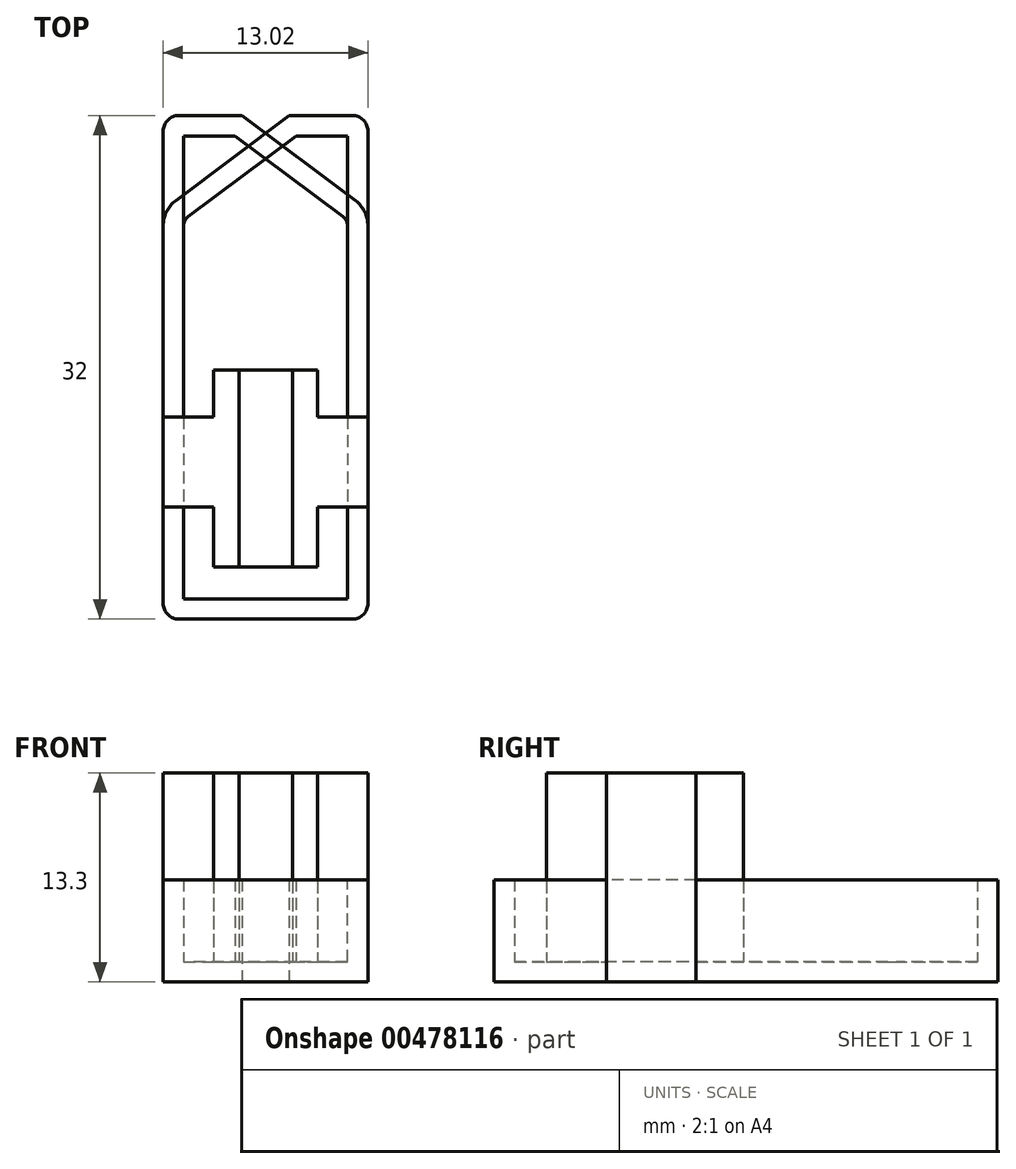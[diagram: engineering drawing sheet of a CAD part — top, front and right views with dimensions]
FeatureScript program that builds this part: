
annotation { "Feature Type Name" : "Feature", "Feature Type Description" : "" }
export const myFeature = defineFeature(function(context is Context, id is Id, definition is map)
    precondition{}
    {
        {
            var Q0;
            Q0=qCreatedBy(makeId("Top.planeOp"),FACE);
            var sketch = newSketch(context, id + "F0", { "sketchPlane" : qUnion([Q0])});
            skLineSegment(sketch, "E0.top", {"start": v(5.5, -13) * mm, "end": v(-5.5, -13) * mm});
            skLineSegment(sketch, "E0.left", {"start": v(6.5, 12) * mm, "end": v(6.5, -12) * mm});
            skLineSegment(sketch, "E0.right", {"start": v(-6.5, 13) * mm, "end": v(-6.5, -12) * mm});
            skPoint(sketch, "E0.middle", {"position": v(0, 0) * mm});
            skLineSegment(sketch, "E1", {"start": v(-6.5, 13) * mm, "end": v(-6.5, 18) * mm});
            skLineSegment(sketch, "E2", {"start": v(-5.5, 19) * mm, "end": v(-1.5, 19) * mm});
            skLineSegment(sketch, "E3", {"start": v(-1.5, 19) * mm, "end": v(5.7, 13.6) * mm});
            skPoint(sketch, "E4.visualSharp", {"position": v(6.5, 13) * mm});
            skArc(sketch, "E4.filletArc", {"start": v(6.5, 12) * mm, "mid": v(6.29, 12.9) * mm, "end": v(5.7, 13.6) * mm});
            skPoint(sketch, "E5.visualSharp", {"position": v(6.5, -13) * mm});
            skArc(sketch, "E5.filletArc", {"start": v(5.5, -13) * mm, "mid": v(6.2, -12.7) * mm, "end": v(6.5, -12) * mm});
            skPoint(sketch, "E6.visualSharp", {"position": v(-6.5, -13) * mm});
            skArc(sketch, "E6.filletArc", {"start": v(-6.5, -12) * mm, "mid": v(-6.2, -12.7) * mm, "end": v(-5.5, -13) * mm});
            skPoint(sketch, "E7.visualSharp", {"position": v(-6.5, 19) * mm});
            skArc(sketch, "E7.filletArc", {"start": v(-5.5, 19) * mm, "mid": v(-6.2, 18.7) * mm, "end": v(-6.5, 18) * mm});
            skSolve(sketch);
        }
        {
            var Q0;
            Q0 = qSketchRegion(id + "F0", true);
            extrude(context, id + "F1", {"entities" : qUnion([Q0]), "depth" : 6.5 * mm});
        }
        {
            var Q0;
            Q0=makeQuery(id+"F1.opExtrude","CAP_FACE",FACE,{"disambiguationData":[OSD([sQuery(id+"F0.wireOp",EDGE,"E0.top"),sQuery(id+"F0.wireOp",EDGE,"E0.left"),sQuery(id+"F0.wireOp",EDGE,"E0.right"),sQuery(id+"F0.wireOp",EDGE,"E1"),sQuery(id+"F0.wireOp",EDGE,"E2"),sQuery(id+"F0.wireOp",EDGE,"E3"),sQuery(id+"F0.wireOp",EDGE,"E4.filletArc"),sQuery(id+"F0.wireOp",EDGE,"E5.filletArc"),sQuery(id+"F0.wireOp",EDGE,"E6.filletArc"),sQuery(id+"F0.wireOp",EDGE,"E7.filletArc")])],"isStart":false});
            shell(context, id + "F2", {"entities" : qUnion([Q0]), "thickness" : 1.3 * mm});
        }
        {
            var Q0;
            Q0=qCreatedBy(makeId("Top.planeOp"),FACE);
            var sketch = newSketch(context, id + "F3", { "sketchPlane" : qUnion([Q0])});
            skLineSegment(sketch, "E8", {"start": v(1.7, -9.67) * mm, "end": v(1.7, 2.83) * mm});
            skLineSegment(sketch, "E9", {"start": v(1.7, 2.83) * mm, "end": v(-3.3, 2.83) * mm});
            skLineSegment(sketch, "E10", {"start": v(-3.3, 2.83) * mm, "end": v(-3.3, -0.17) * mm});
            skLineSegment(sketch, "E11", {"start": v(-3.3, -0.17) * mm, "end": v(-6.51, -0.17) * mm});
            skLineSegment(sketch, "E12", {"start": v(-6.51, -0.17) * mm, "end": v(-6.51, -5.87) * mm});
            skLineSegment(sketch, "E13", {"start": v(-6.51, -5.87) * mm, "end": v(-3.3, -5.87) * mm});
            skLineSegment(sketch, "E14", {"start": v(-3.3, -5.87) * mm, "end": v(-3.3, -9.67) * mm});
            skLineSegment(sketch, "E15", {"start": v(-3.3, -9.67) * mm, "end": v(1.7, -9.67) * mm});
            skSolve(sketch);
        }
        {
            var Q0;
            Q0 = qSketchRegion(id + "F3", true);
            var Q1;
            Q1 = qSketchRegion(id + "F5", true);
            extrude(context, id + "F4", {"entities" : qUnion([Q0, Q1]), "operationType" : NewBodyOperationType.ADD, "depth" : 13.3 * mm});
        }
        {
            var Q0;
            Q0=qCreatedBy(makeId("Top.planeOp"),FACE);
            var sketch = newSketch(context, id + "F5", { "sketchPlane" : qUnion([Q0])});
            skSolve(sketch);
        }
        {
            var Q0;
            Q0=makeQuery(id+"F1.opExtrude","SWEPT_BODY",BODY,{"disambiguationData":[OSD([sQuery(id+"F0.wireOp",EDGE,"E0.top"),sQuery(id+"F0.wireOp",EDGE,"E0.left"),sQuery(id+"F0.wireOp",EDGE,"E0.right"),sQuery(id+"F0.wireOp",EDGE,"E1"),sQuery(id+"F0.wireOp",EDGE,"E2"),sQuery(id+"F0.wireOp",EDGE,"E3"),sQuery(id+"F0.wireOp",EDGE,"E4.filletArc"),sQuery(id+"F0.wireOp",EDGE,"E5.filletArc"),sQuery(id+"F0.wireOp",EDGE,"E6.filletArc"),sQuery(id+"F0.wireOp",EDGE,"E7.filletArc")])]});
            var Q1;
            Q1=qCreatedBy(makeId("Right.planeOp"),FACE);
            mirror(context, id + "F6", {"entities" : qUnion([Q0]), "mirrorPlane" : qUnion([Q1])});
        }
    });
